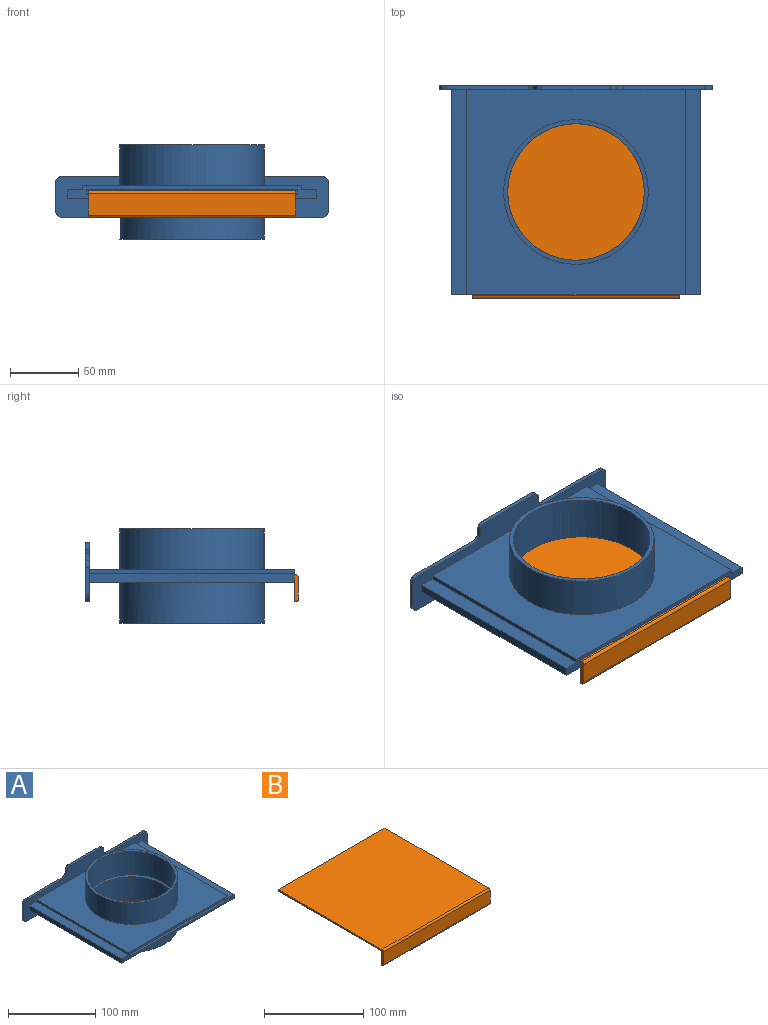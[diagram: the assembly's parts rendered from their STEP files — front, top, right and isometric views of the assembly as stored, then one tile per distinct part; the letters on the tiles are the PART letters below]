
ASSEMBLY  parts=2 mates=1
PART A: 38 faces, bbox 200x153x69 mm
  f0: plane 150x6mm, normal (1,0,0), area 900.3mm2, adj f1,f7,f11,f15
  f1: plane 150x11mm, normal (0,0,1), area 1650mm2, adj f0,f2,f11,f15
  f2: plane 150x3mm, normal (1,0,0), area 449.7mm2, adj f1,f3,f11,f15
  f3: plane 160x150mm, normal (0,0,1), area 15175.3mm2, adj f2,f4,f11,f15,f34
  f4: plane 150x3mm, normal (-1,0,0), area 449.7mm2, adj f3,f5,f11,f15
  f5: plane 150x11mm, normal (0,0,1), area 1650mm2, adj f4,f6,f11,f15
  f6: plane 150x6mm, normal (-1,0,0), area 900.3mm2, adj f5,f7,f11,f15
  f7: plane 182x150mm, normal (0,0,-1), area 18475.3mm2, adj f0,f6,f11,f15,f36
  f8: plane 150x3mm, normal (1,0,0), area 450mm2, adj f9,f11,f12,f25
  f9: plane 154x150mm, normal (0,0,-1), area 15246mm2, adj f8,f10,f11,f14,f25
  f10: plane 150x3mm, normal (-1,0,0), area 450mm2, adj f9,f11,f12,f25
  f11: plane 182x9mm, normal (0,-1,0), area 1110mm2, adj f0,f1,f2,f3,f4,f5,f6,f7
  f12: plane 154x150mm, normal (0,0,1), area 15246mm2, adj f8,f10,f11,f13,f25
  f13: cylinder r=50mm len=100mm, axis (0,0,1), area 10367.3mm2, adj f12,f37
  f14: cylinder r=50mm len=100mm, axis (0,0,1), area 10367.3mm2, adj f9,f35
  f15: plane 200x43.02mm, normal (0,-1,0), area 5187.5mm2, adj f0,f1,f2,f3,f4,f5,f6,f7
  f16: plane 200x43.02mm, normal (0,1,0), area 6759.6mm2, adj f17,f18,f19,f20,f21,f22,f23,f24
  f17: plane 50x3mm, normal (0,0,1), area 150mm2, adj f15,f16,f32,f33
  f18: plane 3.02x3mm, normal (1,0,0), area 9.1mm2, adj f15,f16,f31,f32
  f19: plane 60x3mm, normal (0,0,1), area 180mm2, adj f15,f16,f30,f31
  f20: plane 20x3mm, normal (1,0,0), area 60mm2, adj f15,f16,f29,f30
  f21: plane 190x3mm, normal (0,0,-1), area 570mm2, adj f15,f16,f28,f29
  f22: plane 20x3mm, normal (-1,0,0), area 60mm2, adj f15,f16,f27,f28
  f23: plane 60x3mm, normal (0,0,1), area 180mm2, adj f15,f16,f26,f27
  f24: plane 3.02x3mm, normal (-1,0,0), area 9.1mm2, adj f15,f16,f26,f33
  f25: plane 154x3mm, normal (0,-1,0), area 462mm2, adj f8,f9,f10,f12
  f26: cylinder r=5mm len=5mm, axis (0,-1,0), area 23.6mm2, adj f15,f16,f23,f24
  f27: cylinder r=5mm len=5mm, axis (0,-1,0), area 23.6mm2, adj f15,f16,f22,f23
  f28: cylinder r=5mm len=5mm, axis (0,1,0), area 23.6mm2, adj f15,f16,f21,f22
  f29: cylinder r=5mm len=5mm, axis (0,-1,0), area 23.6mm2, adj f15,f16,f20,f21
  f30: cylinder r=5mm len=5mm, axis (0,-1,0), area 23.6mm2, adj f15,f16,f19,f20
  f31: cylinder r=5mm len=5mm, axis (0,-1,0), area 23.6mm2, adj f15,f16,f18,f19
  f32: cylinder r=5mm len=5mm, axis (0,1,0), area 23.6mm2, adj f15,f16,f17,f18
  f33: cylinder r=5mm len=5mm, axis (0,-1,0), area 23.6mm2, adj f15,f16,f17,f24
  f34: cylinder r=53mm len=106mm, axis (0,0,-1), area 9990.3mm2, adj f3,f35
  f35: plane 106x106mm, normal (0,0,1), area 970.8mm2, adj f14,f34
  f36: cylinder r=53mm len=106mm, axis (0,0,1), area 9990.3mm2, adj f7,f37
  f37: plane 106x106mm, normal (0,0,-1), area 970.8mm2, adj f13,f36
PART B: 10 faces, bbox 152x150x20 mm
  f0: plane 150x20mm, normal (1,0,0), area 352.3mm2, adj f1,f3,f4,f5,f6,f7,f8,f9
  f1: plane 152x2mm, normal (0,1,0), area 304mm2, adj f0,f2,f3,f4
  f2: plane 150x20mm, normal (-1,0,0), area 352.3mm2, adj f1,f3,f4,f5,f6,f7,f8,f9
  f3: plane 152x147mm, normal (0,0,-1), area 22344mm2, adj f0,f1,f2,f5
  f4: plane 152x148mm, normal (0,0,1), area 22496mm2, adj f0,f1,f2,f8
  f5: plane 152x18mm, normal (0,1,0), area 2736mm2, adj f0,f2,f3,f7
  f6: plane 152x16mm, normal (0,-1,0), area 2432mm2, adj f0,f2,f8,f9
  f7: plane 152x1mm, normal (0,0,-1), area 152mm2, adj f0,f2,f5,f9
  f8: cylinder r=2mm len=152mm, axis (1,0,0), area 477.5mm2, adj f0,f2,f4,f6
  f9: cylinder r=2mm len=152mm, axis (-1,0,0), area 477.5mm2, adj f0,f2,f6,f7
PLACE A t=(-47.76,-66.38,43.14)mm fixed
PLACE B t=(-47.76,-144.38,42.63)mm
MATE slider A.f11 <-> B.f1  axis (0,-1,0) through (-124.76,-216.38,40.13)mm
